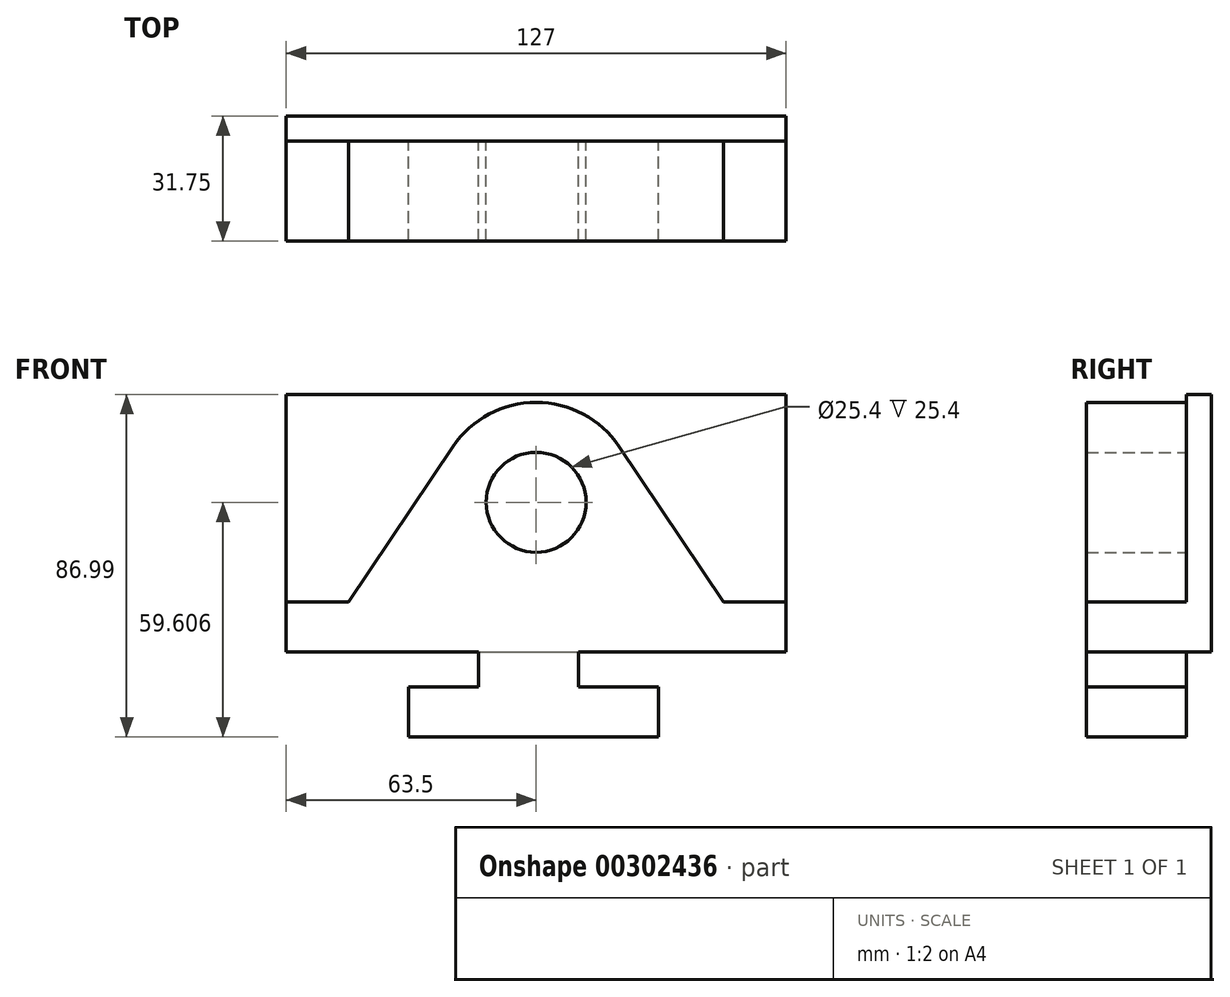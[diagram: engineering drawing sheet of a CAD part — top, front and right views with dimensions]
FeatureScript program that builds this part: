
annotation { "Feature Type Name" : "Feature", "Feature Type Description" : "" }
export const myFeature = defineFeature(function(context is Context, id is Id, definition is map)
    precondition{}
    {
        {
            var Q0;
            Q0=qCreatedBy(makeId("Front.planeOp"),FACE);
            var sketch = newSketch(context, id + "F0", { "sketchPlane" : qUnion([Q0])});
            skLineSegment(sketch, "E0.bottom", {"start": v(0, 0) * mm, "end": v(48.85, 0) * mm});
            skLineSegment(sketch, "E0.top", {"start": v(0, 63.5) * mm, "end": v(127, 63.5) * mm});
            skLineSegment(sketch, "E0.left", {"start": v(0, 0) * mm, "end": v(0, 63.5) * mm});
            skLineSegment(sketch, "E0.right", {"start": v(127, 0) * mm, "end": v(127, 63.5) * mm});
            skLineSegment(sketch, "E1", {"start": v(0, 12.7) * mm, "end": v(15.87, 12.7) * mm});
            skLineSegment(sketch, "E2", {"start": v(15.87, 12.7) * mm, "end": v(42.42, 52.19) * mm});
            skLineSegment(sketch, "E3", {"start": v(127, 12.7) * mm, "end": v(111.13, 12.7) * mm});
            skLineSegment(sketch, "E4", {"start": v(111.12, 12.7) * mm, "end": v(84.58, 52.19) * mm});
            skLineSegment(sketch, "E5", {"start": v(48.85, 0) * mm, "end": v(48.85, -8.9) * mm});
            skLineSegment(sketch, "E6", {"start": v(48.85, -8.9) * mm, "end": v(31.06, -8.9) * mm});
            skLineSegment(sketch, "E7", {"start": v(31.06, -8.9) * mm, "end": v(31.06, -21.59) * mm});
            skLineSegment(sketch, "E8", {"start": v(31.06, -21.6) * mm, "end": v(94.56, -21.6) * mm});
            skLineSegment(sketch, "E9", {"start": v(94.56, -21.6) * mm, "end": v(94.56, -8.9) * mm});
            skLineSegment(sketch, "E10", {"start": v(94.56, -8.9) * mm, "end": v(74.25, -8.9) * mm});
            skLineSegment(sketch, "E11", {"start": v(74.25, -8.9) * mm, "end": v(74.25, 0) * mm});
            skLineSegment(sketch, "E12.trimOffspring", {"start": v(74.25, 0) * mm, "end": v(127, 0) * mm});
            skArc(sketch, "E13", {"start": v(84.58, 52.19) * mm, "mid": v(63.5, 63.42) * mm, "end": v(42.42, 52.19) * mm});
            skCircle(sketch, "E14", {"center": v(63.5, 38.02) * mm, "radius": 12.7 * mm});
            skSolve(sketch);
        }
        {
            var Q0;
            {var subQ1=sQuery(id+"F0.wireOp",EDGE,"E0.bottom");Q0=makeQuery(id+"F0.imprint","IMPRINT",FACE,{"disambiguationData":[TD([[makeQuery(id+"F0.imprint","IMPRINT",EDGE,{"derivedFrom":subQ1}),1.0]])]});}
            extrude(context, id + "F1", {"entities" : qUnion([Q0]), "depth" : 25.4 * mm});
        }
        {
            var Q0;
            Q0=makeQuery(id+"F1.opExtrude","CAP_FACE",FACE,{"disambiguationData":[OSD([sQuery(id+"F0.wireOp",EDGE,"E0.bottom"),sQuery(id+"F0.wireOp",EDGE,"E0.left"),sQuery(id+"F0.wireOp",EDGE,"E0.right"),sQuery(id+"F0.wireOp",EDGE,"E1"),sQuery(id+"F0.wireOp",EDGE,"E2"),sQuery(id+"F0.wireOp",EDGE,"E3"),sQuery(id+"F0.wireOp",EDGE,"E4"),sQuery(id+"F0.wireOp",EDGE,"E5"),sQuery(id+"F0.wireOp",EDGE,"E6"),sQuery(id+"F0.wireOp",EDGE,"E7"),sQuery(id+"F0.wireOp",EDGE,"E8"),sQuery(id+"F0.wireOp",EDGE,"E9"),sQuery(id+"F0.wireOp",EDGE,"E10"),sQuery(id+"F0.wireOp",EDGE,"E11"),sQuery(id+"F0.wireOp",EDGE,"E12.trimOffspring"),sQuery(id+"F0.wireOp",EDGE,"E13"),sQuery(id+"F0.wireOp",EDGE,"E14")])],"isStart":true});
            var sketch = newSketch(context, id + "F2", { "sketchPlane" : qUnion([Q0])});
            skLineSegment(sketch, "E15.bottom", {"start": v(-127, 0) * mm, "end": v(0, 0) * mm});
            skLineSegment(sketch, "E15.top", {"start": v(-127, 65.4) * mm, "end": v(0, 65.4) * mm});
            skLineSegment(sketch, "E15.left", {"start": v(-127, 0) * mm, "end": v(-127, 65.4) * mm});
            skLineSegment(sketch, "E15.right", {"start": v(0, 0) * mm, "end": v(0, 65.4) * mm});
            skSolve(sketch);
        }
        {
            var Q0;
            Q0 = qSketchRegion(id + "F2", true);
            extrude(context, id + "F3", {"entities" : qUnion([Q0]), "operationType" : NewBodyOperationType.ADD, "depth" : 6.35 * mm});
        }
    });
